# Revit family: ABRFB1480xxWSxM9x
name_source: partatom
category: Leuchten
units: mm (PartAtom-declared; Revit-internal decimal feet)

## family parameters
Basisbauteil = Fläche
Beim Laden mit Abzugskörper schneiden = Nein
Bemaßung runder Anschluss = Durchmesser verwenden
Gemeinsam genutzt = Nein
Lichtquelle = Ja
OmniClass-Nummer = 23.80.70.11
OmniClass-Titel = Luminaries for Internal Lighting
Raumberechnungspunkt = Nein
Teiletyp = Normal

## types (6) — shared parameters
Baugruppenkennzeichen = D5020200
Emissionsform beim Rendern sichtbar = Nein
Farbfilter = 16777215
Farbtemperaturverschiebung bei Dämpfen der Lampe = <Keine Auswahl>
Hersteller = RIDI Leuchten GmbH
Lampe = LED
Neigungswinkel = 90.00°
Scheinlast = 41 VA
URL = www.ridi.de
Von Breite des Rechtecks ausssenden = 1440 mm  [stored 4.72441 ft]
Von Länge des Rechtecks aussenden = 92 mm  [stored 0.301837 ft]
brand = RIDI
conformity mark = CE
electrical safety class = 1
height = 60 mm  [stored 0.19685 ft]
ingress protection (IP) code = IP20
length = 1480 mm  [stored 4.85564 ft]
nominal frequency = 50-60Hz
nominal voltage = 230
rated input power = 41
voltage type (AC, DC, UC) = AC
width = 131 mm  [stored 0.42979 ft]
zero-valued in all types: Vorgabe-Ansicht

## per-type parameters (varying)
| type | Datei für fotometrisches Netz | Modell | weight |
| ABRFB1480NDWS840M9S0600 | xxxM9Sxxx.IES | 0627871 | 4,67kg |
| ABRFB1480DAWS840M9S0600 | xxxM9Sxxx.IES | 0637871 | 4,67kg |
| ABRFB1480RFWS840M9P0700 | xxxM9Pxxx.IES | 0627875 | 4,69kg |
| ABRFB1480DAWS840M9P0700 | xxxM9Pxxx.IES | 0637875 | 4,67kg |
| ABRFB1480RFWS940M9P0550 | xxxM9Pxxx.IES | 0627876 | 4,69kg |
| ABRFB1480DAWS940M9P0550 | xxxM9Pxxx.IES | 0637876 | 4,67kg |

note: column(s) folded — value = type name in every type: product name

note: [stored X ft] marks values corroborated as IEEE doubles in the binary element streams (Revit-internal decimal feet)
